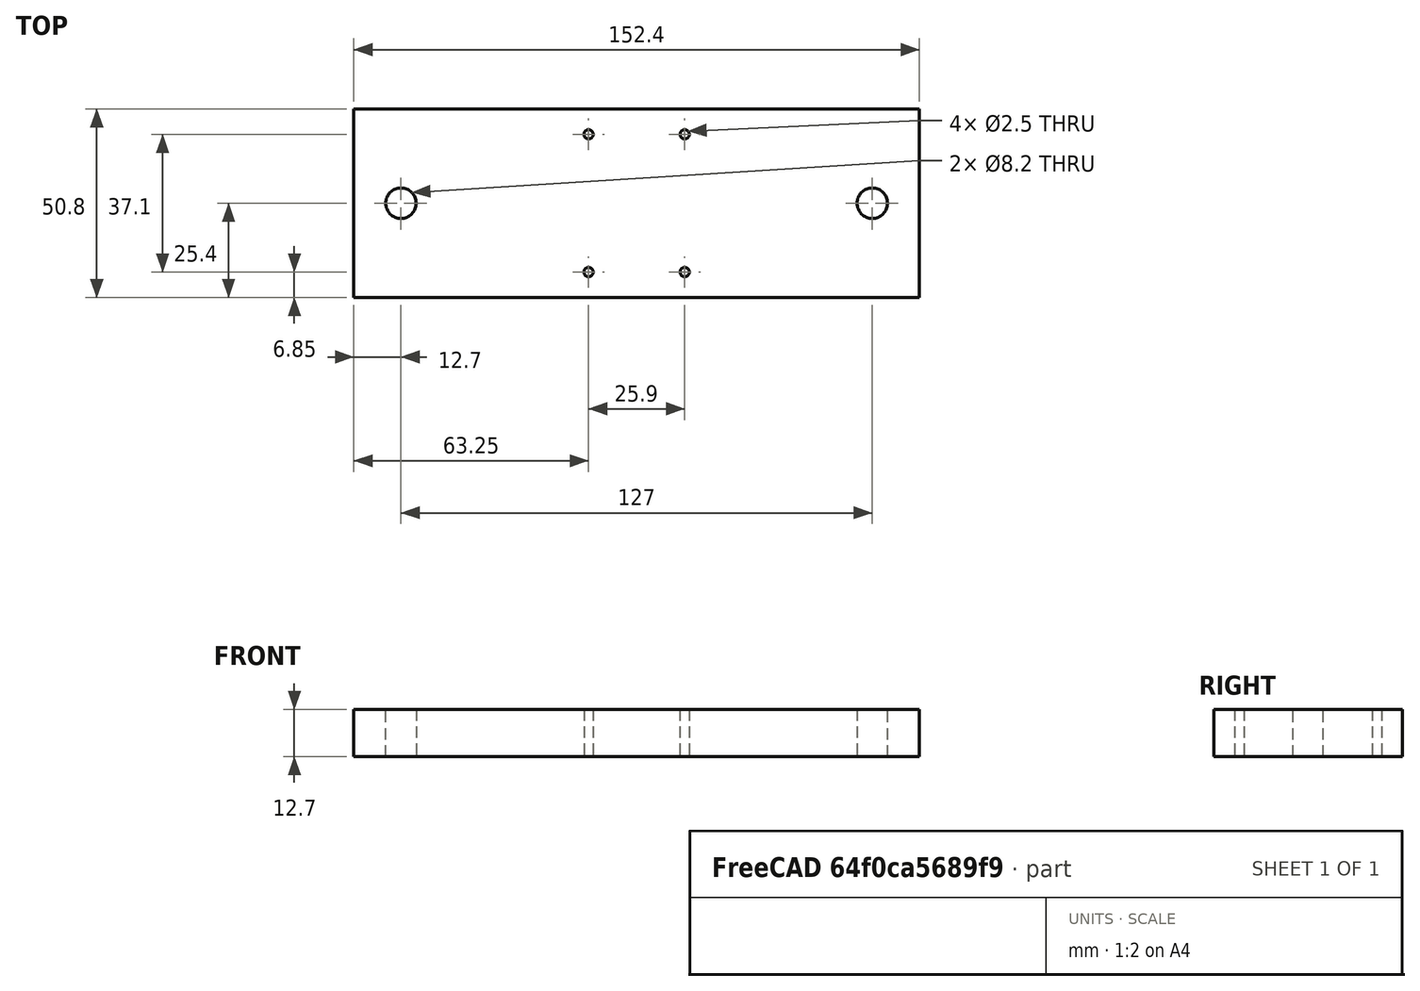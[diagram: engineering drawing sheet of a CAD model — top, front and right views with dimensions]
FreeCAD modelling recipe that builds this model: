
FCSTD DOCUMENT  (FreeCAD 0.17R13522 (Git))
Label: Machining_Fixture
License: All rights reserved
LicenseURL: http://en.wikipedia.org/wiki/All_rights_reserved
objects: TechDraw::DrawViewDimension×8, Sketcher::SketchObject×3, PartDesign::Mirrored×3, TechDraw::DrawProjGroupItem×2, PartDesign::Pad×1, PartDesign::Pocket×1, PartDesign::Hole×1, PartDesign::MultiTransform×1, PartDesign::Body×1, TechDraw::DrawSVGTemplate×1, TechDraw::DrawProjGroup×1, TechDraw::DrawPage×1
note: 14 computed .brp shape members not serialized (recipe doc carries the construction recipe); baked Part::Feature solids carry a one-line shape summary decoded from their .brp

FEATURE [Sketcher::SketchObject] Sketch
  MapMode = 5
  Support = -> [XY_Plane]
  sketch-geometry (4):
    g0: LineSegment StartX=-76.2 StartY=25.4 StartZ=0 EndX=76.2 EndY=25.4 EndZ=0
    g1: LineSegment StartX=76.2 StartY=25.4 StartZ=0 EndX=76.2 EndY=-25.4 EndZ=0
    g2: LineSegment StartX=76.2 StartY=-25.4 StartZ=0 EndX=-76.2 EndY=-25.4 EndZ=0
    g3: LineSegment StartX=-76.2 StartY=-25.4 StartZ=0 EndX=-76.2 EndY=25.4 EndZ=0
  constraints (12):
    c: Coincident(g0,g1)
    c: Coincident(g1,g2)
    c: Coincident(g2,g3)
    c: Coincident(g3,g0)
    c: Horizontal(g0)
    c: Horizontal(g2)
    c: Vertical(g1)
    c: Vertical(g3)
    c: DistanceY(g1,g1) = 50.8
    c: DistanceX(g0,g0) = 152.4
    c: Symmetric(g0,g1,g-1)
    c: Symmetric(g0,g0,g-2)
FEATURE [PartDesign::Pad] Pad
  Length = 12.7
  Length2 = 100
  Profile = -> Sketch
  Refine = true
  Reversed = true
  Type = 0
FEATURE [Sketcher::SketchObject] Sketch001
  ExternalGeometry = -> [Pad]
  MapMode = 5
  Support = -> [Pad]
  expr: Constraints[4] = 0.32300000000000001in / 2
  expr: Constraints[2] = 1 / 2 * 1in
  expr: Constraints[1] = 14.25 / 2
  sketch-geometry (2):
    g0: Circle [constr] CenterX=-63.5 CenterY=0 CenterZ=0 NormalX=0 NormalY=0 NormalZ=1 AngleXU=0 Radius=7.125
    g1: Circle CenterX=-63.5 CenterY=0 CenterZ=0 NormalX=0 NormalY=0 NormalZ=1 AngleXU=0 Radius=4.1021
  constraints (5):
    c: PointOnObject(g0,g-1)
    c: Radius(g0) = 7.125
    c: DistanceX(g-3,g0) = 12.7
    c: Coincident(g1,g0)
    c: Radius(g1) = 4.1021
FEATURE [PartDesign::Pocket] Pocket
  BaseFeature = -> Pad
  Length = 5
  Length2 = 100
  Profile = -> Sketch001
  Refine = true
  Type = 1
FEATURE [PartDesign::Mirrored] Mirrored
  BaseFeature = -> Pocket
  MirrorPlane = -> YZ_Plane
  Originals = -> [Pocket]
  Refine = true
FEATURE [Sketcher::SketchObject] Sketch002
  MapMode = 5
  Support = -> [Mirrored]
  expr: Constraints[2] = (44.399999999999999 - 18.5) / 2
  expr: Constraints[1] = 37.100000000000001 / 2
  expr: Constraints[0] = 2.5 / 2
  sketch-geometry (1):
    g0: Circle CenterX=12.95 CenterY=18.55 CenterZ=0 NormalX=0 NormalY=0 NormalZ=1 AngleXU=0 Radius=1.25
  constraints (3):
    c: Radius(g0) = 1.25
    c: DistanceY(g-1,g0) = 18.55
    c: DistanceX(g-1,g0) = 12.95
FEATURE [PartDesign::Hole] Hole
  BaseFeature = -> Mirrored
  Depth = 25
  DepthType = 1
  Diameter = 2.5
  DrillPoint = 1
  DrillPointAngle = 118
  HoleCutCountersinkAngle = 90
  HoleCutDepth = 0
  HoleCutDiameter = 3
  HoleCutType = 0
  ModelActualThread = false
  Profile = -> Sketch002
  Refine = true
  Tapered = false
  TaperedAngle = 90
  ThreadAngle = 60
  ThreadClass = 0
  ThreadCutOffInner = 0.0541266
  ThreadCutOffOuter = 0.108253
  ThreadDirection = 1
  ThreadFit = 0
  ThreadPitch = 0.5
  ThreadSize = 3
  ThreadType = 1
  Threaded = true
FEATURE [PartDesign::Mirrored] Mirrored001
  MirrorPlane = -> YZ_Plane
  Refine = true
FEATURE [PartDesign::Mirrored] Mirrored002
  MirrorPlane = -> XZ_Plane
  Refine = true
FEATURE [PartDesign::MultiTransform] MultiTransform
  BaseFeature = -> Hole
  Originals = -> [Hole]
  Refine = true
  Transformations = -> [Mirrored001,Mirrored002]
FEATURE [PartDesign::Body] Body
  Group = -> [Sketch,Pad,Sketch001,Pocket,Mirrored,Sketch002,Hole,MultiTransform,Mirrored001,Mirrored002]
  Origin = -> Origin
  Tip = -> MultiTransform
FEATURE [TechDraw::DrawSVGTemplate] Template
  EditableTexts = Code=Code; CompanyName=Perry Leumas; DrawingNumber=Drawing Number; DrawingTitle1=Enclosure Machining Fixture; DrawingTitle2=0.5&quot; x 2&quot; Aluminum 6061-T6511; DrawnBy=S. Perry; Revision=Rev; Scale=1:1; Sheet=Sheet n of m; Weight=Weight
  Height = 215.9
  Orientation = 1
  Width = 279.4
FEATURE [TechDraw::DrawProjGroupItem] ProjItem  label="Front"
  CoarseView = false
  Direction = (0,0,-1)
  Focus = 100
  HardHidden = false
  IsoCount = 0
  IsoHidden = false
  IsoVisible = false
  LockPosition = true
  Perspective = false
  Rotation = 0
  RotationVector = (1,0,0)
  ScaleType = 0
  SeamHidden = false
  SeamVisible = false
  SmoothHidden = false
  SmoothVisible = false
  Source = -> [MultiTransform]
  Type = 0
  X = 0
  Y = 0
FEATURE [TechDraw::DrawProjGroupItem] ProjItem001  label="Left"
  CoarseView = false
  Direction = (-1,0,0)
  Focus = 100
  HardHidden = false
  IsoCount = 0
  IsoHidden = false
  IsoVisible = false
  LockPosition = true
  Perspective = false
  Rotation = 0
  RotationVector = (0,0,-1)
  ScaleType = 0
  SeamHidden = false
  SeamVisible = false
  SmoothHidden = false
  SmoothVisible = false
  Source = -> [MultiTransform]
  Type = 1
  X = 108.585
  Y = 0
FEATURE [TechDraw::DrawProjGroup] ProjGroup
  Anchor = -> ProjItem
  AutoDistribute = true
  CubeDirs = (6) [(0,1,-6.12323e-17),(0,-6.12323e-17,-1),(-1,0,0),(0,6.12323e-17,1),(1,0,0),(0,-1,6.12323e-17)]
  CubeRotations = (6) [(1,0,0),(1,0,0),(0,6.12323e-17,-1),(-1,0,0),(0,-6.12323e-17,1),(1,0,0)]
  LockPosition = false
  ProjectionType = 0
  Rotation = 0
  ScaleType = 0
  Source = -> [MultiTransform]
  Views = -> [ProjItem,ProjItem001]
  X = 126.429
  Y = 96.6615
  spacingX = 15
  spacingY = 15
FEATURE [TechDraw::DrawViewDimension] Dimension
  FormatSpec = %.2f
  LockPosition = false
  MeasureType = 1
  References2D = -> [ProjItem]
  Rotation = 0
  ScaleType = 0
  Type = 1
  X = 0.735187
  Y = 44.1112
FEATURE [TechDraw::DrawViewDimension] Dimension001
  FormatSpec = %.2f
  LockPosition = false
  MeasureType = 1
  References2D = -> [ProjItem]
  Rotation = 0
  ScaleType = 0
  Type = 2
  X = -27.5909
  Y = 1.4914
FEATURE [TechDraw::DrawViewDimension] Dimension002
  FormatSpec = %.2f
  LockPosition = false
  MeasureType = 1
  References2D = -> [ProjItem]
  Rotation = 0
  ScaleType = 0
  Type = 1
  X = 1.67783
  Y = 55.5547
FEATURE [TechDraw::DrawViewDimension] Dimension003
  FormatSpec = %.2f
  LockPosition = false
  MeasureType = 1
  References2D = -> [ProjItem]
  Rotation = 0
  ScaleType = 0
  Type = 2
  X = -86.3149
  Y = 1.30498
FEATURE [TechDraw::DrawViewDimension] Dimension004
  FormatSpec = %.2f
  LockPosition = false
  MeasureType = 1
  References2D = -> [ProjItem001]
  Rotation = 0
  ScaleType = 0
  Type = 1
  X = -18.0833
  Y = 44.9285
FEATURE [TechDraw::DrawViewDimension] Dimension005
  FormatSpec = 4X M3x0.5 %.2f 
  LockPosition = false
  MeasureType = 1
  References2D = -> [ProjItem]
  Rotation = 0
  ScaleType = 0
  Type = 5
  X = 53.6346
  Y = 35.5779
FEATURE [TechDraw::DrawViewDimension] Dimension006
  FormatSpec = %.2f
  LockPosition = false
  MeasureType = 1
  References2D = -> [ProjItem]
  Rotation = 0
  ScaleType = 0
  Type = 5
  X = -38.9649
  Y = 15.684
FEATURE [TechDraw::DrawViewDimension] Dimension007
  FormatSpec = %.2f
  LockPosition = false
  MeasureType = 1
  References2D = -> [ProjItem]
  Rotation = 0
  ScaleType = 0
  Type = 1
  X = -46.7927
  Y = 40.2679
FEATURE [TechDraw::DrawPage] Page
  KeepUpdated = true
  ProjectionType = 0
  Template = -> Template
  Views = -> [ProjGroup,Dimension,Dimension001,Dimension002,Dimension003,Dimension004,Dimension005,Dimension006,Dimension007]
